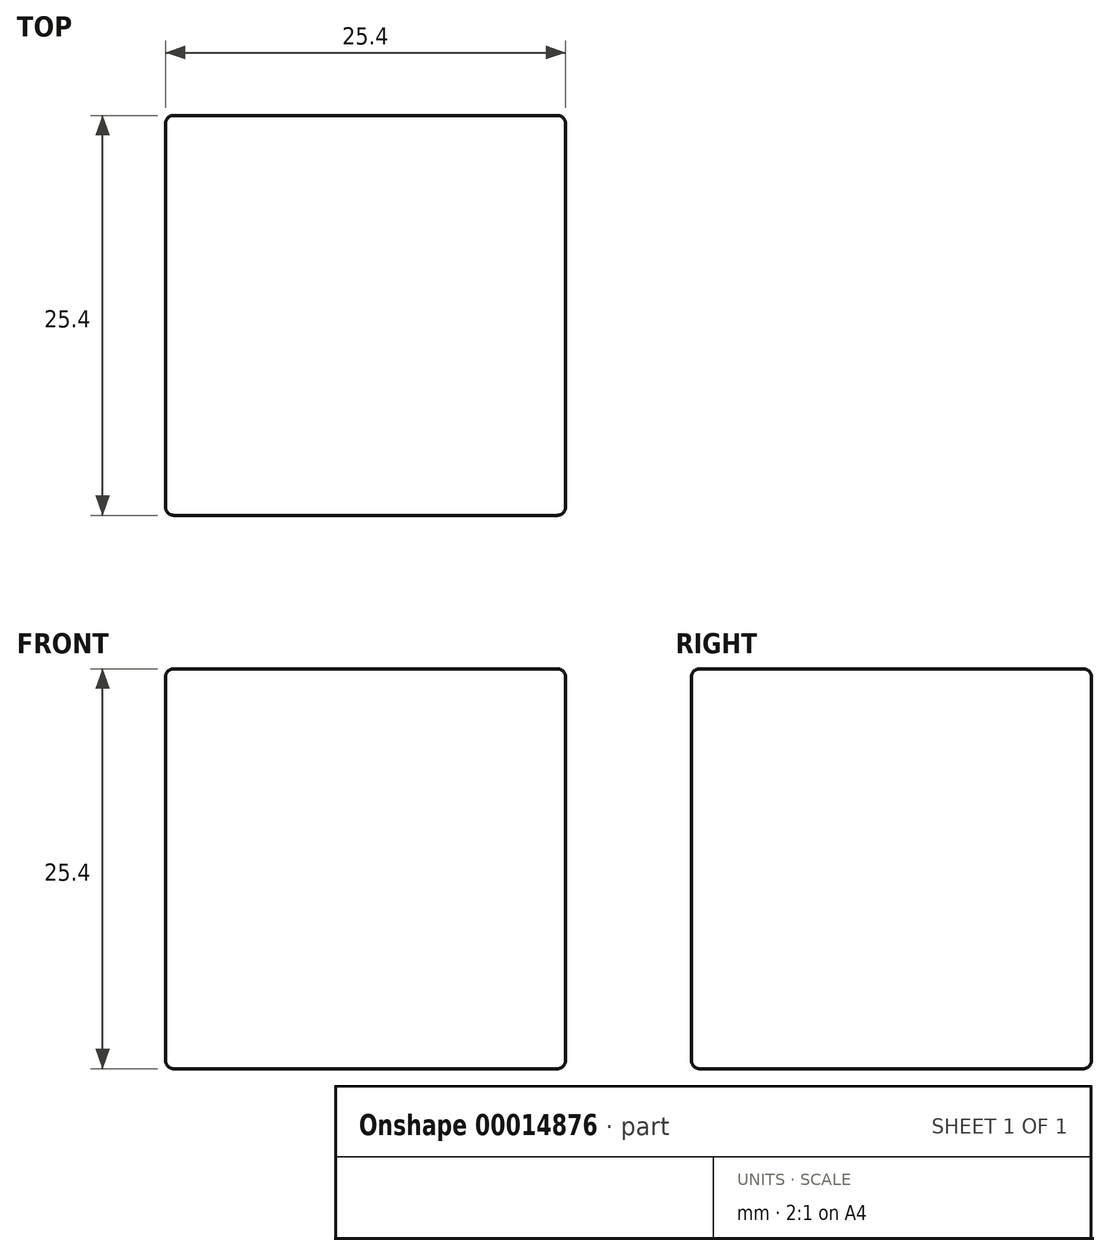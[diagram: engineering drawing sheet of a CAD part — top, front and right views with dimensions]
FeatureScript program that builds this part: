
annotation { "Feature Type Name" : "Feature", "Feature Type Description" : "" }
export const myFeature = defineFeature(function(context is Context, id is Id, definition is map)
    precondition{}
    {
        {
            var Q0;
            Q0=qCreatedBy(makeId("Top.planeOp"),FACE);
            var sketch = newSketch(context, id + "F0", { "sketchPlane" : qUnion([Q0])});
            skLineSegment(sketch, "E0.rect.bottom", {"start": v(12.7, 12.7) * mm, "end": v(-12.7, 12.7) * mm});
            skLineSegment(sketch, "E0.rect.top", {"start": v(12.7, -12.7) * mm, "end": v(-12.7, -12.7) * mm});
            skLineSegment(sketch, "E0.rect.left", {"start": v(12.7, 12.7) * mm, "end": v(12.7, -12.7) * mm});
            skLineSegment(sketch, "E0.rect.right", {"start": v(-12.7, 12.7) * mm, "end": v(-12.7, -12.7) * mm});
            skPoint(sketch, "E0.rect.middle", {"position": v(0, 0) * mm});
            skSolve(sketch);
        }
        {
            var Q0;
            Q0 = qSketchRegion(id + "F0", true);
            extrude(context, id + "F1", {"entities" : qUnion([Q0]), "depth" : 25.4 * mm});
        }
        {
            var Q0;
            Q0=makeQuery(id+"F1.opExtrude","SWEPT_FACE",FACE,{"disambiguationData":[OSD([sQuery(id+"F0.wireOp",EDGE,"E0.rect.bottom")])]});
            var Q1;
            Q1=makeQuery(id+"F1.opExtrude","SWEPT_FACE",FACE,{"disambiguationData":[OSD([sQuery(id+"F0.wireOp",EDGE,"E0.rect.top")])]});
            var Q2;
            Q2=makeQuery(id+"F1.opExtrude","CAP_FACE",FACE,{"disambiguationData":[OSD([sQuery(id+"F0.wireOp",EDGE,"E0.rect.bottom"),sQuery(id+"F0.wireOp",EDGE,"E0.rect.top"),sQuery(id+"F0.wireOp",EDGE,"E0.rect.left"),sQuery(id+"F0.wireOp",EDGE,"E0.rect.right")])],"isStart":true});
            var Q3;
            Q3=makeQuery(id+"F1.opExtrude","CAP_FACE",FACE,{"disambiguationData":[OSD([sQuery(id+"F0.wireOp",EDGE,"E0.rect.bottom"),sQuery(id+"F0.wireOp",EDGE,"E0.rect.top"),sQuery(id+"F0.wireOp",EDGE,"E0.rect.left"),sQuery(id+"F0.wireOp",EDGE,"E0.rect.right")])],"isStart":false});
            fillet(context, id + "F2", {"entities" : qUnion([Q0, Q1, Q2, Q3]), "radius" : 0.5 * mm, "tangentPropagation" : true, "allowEdgeOverflow" : false});
        }
    });
